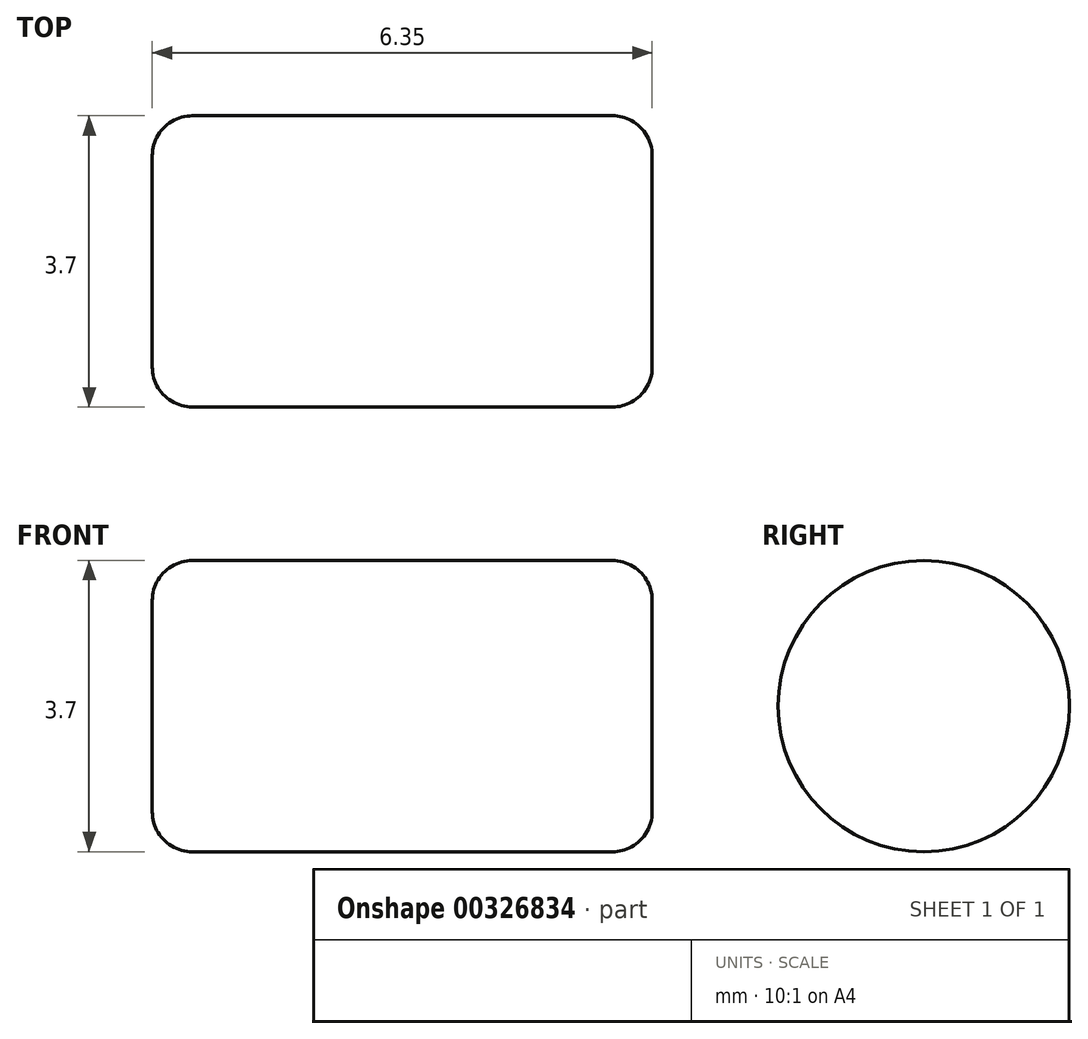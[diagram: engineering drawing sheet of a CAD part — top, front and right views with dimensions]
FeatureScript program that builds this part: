
annotation { "Feature Type Name" : "Feature", "Feature Type Description" : "" }
export const myFeature = defineFeature(function(context is Context, id is Id, definition is map)
    precondition{}
    {
        {
            var Q0;
            Q0=qCreatedBy(makeId("Front.planeOp"),FACE);
            var sketch = newSketch(context, id + "F0", { "sketchPlane" : qUnion([Q0])});
            skLineSegment(sketch, "E0.bottom", {"start": v(0, 0) * mm, "end": v(6.35, 0) * mm});
            skLineSegment(sketch, "E0.top", {"start": v(0, 7.94) * mm, "end": v(6.35, 7.94) * mm});
            skLineSegment(sketch, "E0.left", {"start": v(0, 0) * mm, "end": v(0, 7.94) * mm});
            skLineSegment(sketch, "E0.right", {"start": v(6.35, 0) * mm, "end": v(6.35, 7.94) * mm});
            skLineSegment(sketch, "E1", {"start": v(3.17, 7.94) * mm, "end": v(3.17, 6.75) * mm});
            skCircle(sketch, "E2", {"center": v(3.17, 6.75) * mm, "radius": 1.2 * mm});
            skLineSegment(sketch, "E3", {"start": v(3.17, 7.94) * mm, "end": v(1.59, 7.94) * mm});
            skLineSegment(sketch, "E4", {"start": v(3.17, 7.94) * mm, "end": v(4.76, 7.94) * mm});
            skLineSegment(sketch, "E5", {"start": v(3.17, 6.75) * mm, "end": v(1.98, 6.75) * mm});
            skLineSegment(sketch, "E6", {"start": v(1.98, 6.75) * mm, "end": v(4.37, 6.75) * mm});
            skLineSegment(sketch, "E7", {"start": v(1.59, 7.94) * mm, "end": v(1.98, 6.75) * mm});
            skLineSegment(sketch, "E8", {"start": v(4.76, 7.94) * mm, "end": v(4.37, 6.75) * mm});
            skLineSegment(sketch, "E9", {"start": v(0, 0) * mm, "end": v(0, 1.85) * mm});
            skLineSegment(sketch, "E10", {"start": v(0, 1.85) * mm, "end": v(6.35, 1.85) * mm});
            skLineSegment(sketch, "E11", {"start": v(6.35, 1.85) * mm, "end": v(6.35, 0) * mm});
            skSolve(sketch);
        }
        {
            var Q0;
            {var subQ1=sQuery(id+"F0.wireOp",EDGE,"E0.left");Q0=makeQuery(id+"F0.imprint","IMPRINT",FACE,{"disambiguationData":[TD([[makeQuery(id+"F0.imprint","IMPRINT",EDGE,{"derivedFrom":subQ1}),-1.0]])]});}
            var Q1;
            Q1=sQuery(id+"F0.wireOp",EDGE,"E0.bottom");
            revolve(context, id + "F1", {"entities" : qUnion([Q0]), "axis" : qUnion([Q1]), "revolveType" : RevolveType.FULL});
        }
        {
            var Q0;
            Q0=makeQuery(id+"F1.opRevolve","SWEPT_FACE",FACE,{"disambiguationData":[OSD([sQuery(id+"F0.wireOp",EDGE,"E0.left")])]});
            var Q1;
            Q1=makeQuery(id+"F1.opRevolve","SWEPT_FACE",FACE,{"disambiguationData":[OSD([sQuery(id+"F0.wireOp",EDGE,"E0.right")])]});
            var Q2;
            Q2=makeQuery(id+"F1.opRevolve","SWEPT_EDGE",EDGE,{"disambiguationData":[OSD([sQuery(id+"F0.wireOp",EDGE,"E0.top"),sQuery(id+"F0.wireOp",EDGE,"E3"),sQuery(id+"F0.wireOp",EDGE,"E7")])]});
            var Q3;
            Q3=makeQuery(id+"F1.opRevolve","SWEPT_EDGE",EDGE,{"disambiguationData":[OSD([sQuery(id+"F0.wireOp",EDGE,"E0.top"),sQuery(id+"F0.wireOp",EDGE,"E4"),sQuery(id+"F0.wireOp",EDGE,"E8")])]});
            fillet(context, id + "F2", {"entities" : qUnion([Q0, Q1, Q2, Q3]), "radius" : 0.5 * mm, "tangentPropagation" : true, "allowEdgeOverflow" : false});
        }
    });
